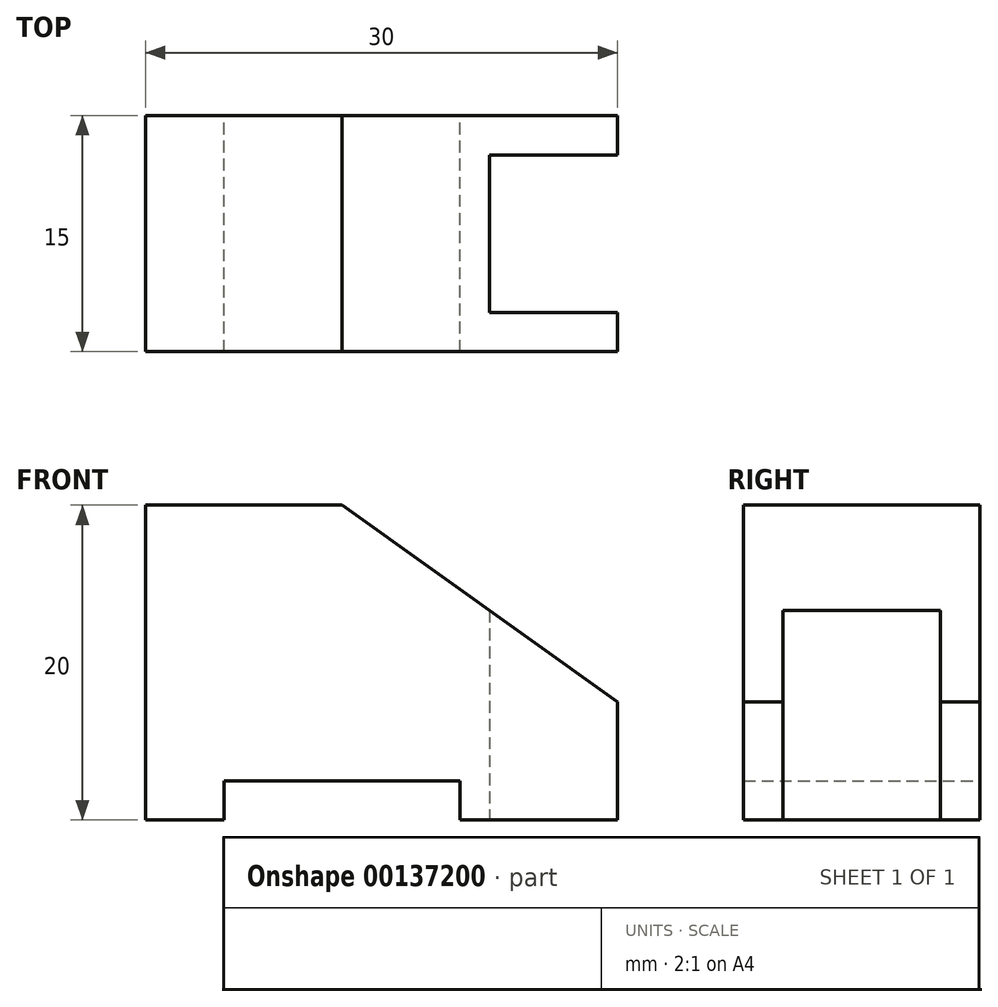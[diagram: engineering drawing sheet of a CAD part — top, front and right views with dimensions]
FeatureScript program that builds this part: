
annotation { "Feature Type Name" : "Feature", "Feature Type Description" : "" }
export const myFeature = defineFeature(function(context is Context, id is Id, definition is map)
    precondition{}
    {
        {
            var Q0;
            Q0=qCreatedBy(makeId("Front.planeOp"),FACE);
            var sketch = newSketch(context, id + "F0", { "sketchPlane" : qUnion([Q0])});
            skLineSegment(sketch, "E0", {"start": v(0, 0) * mm, "end": v(0, 20) * mm});
            skLineSegment(sketch, "E1", {"start": v(0, 20) * mm, "end": v(12.5, 20) * mm});
            skLineSegment(sketch, "E2", {"start": v(12.5, 20) * mm, "end": v(30, 7.5) * mm});
            skLineSegment(sketch, "E3", {"start": v(30, 7.5) * mm, "end": v(30, 0) * mm});
            skLineSegment(sketch, "E4", {"start": v(30, 0) * mm, "end": v(20, 0) * mm});
            skLineSegment(sketch, "E5", {"start": v(20, 0) * mm, "end": v(20, 2.5) * mm});
            skLineSegment(sketch, "E6", {"start": v(20, 2.5) * mm, "end": v(5, 2.5) * mm});
            skLineSegment(sketch, "E7", {"start": v(5, 2.5) * mm, "end": v(5, 0) * mm});
            skLineSegment(sketch, "E8", {"start": v(5, 0) * mm, "end": v(0, 0) * mm});
            skSolve(sketch);
        }
        {
            var Q0;
            Q0 = qSketchRegion(id + "F0", true);
            extrude(context, id + "F1", {"entities" : qUnion([Q0]), "depth" : 15 * mm});
        }
        {
            var Q0;
            Q0=qCreatedBy(makeId("Top.planeOp"),FACE);
            var sketch = newSketch(context, id + "F2", { "sketchPlane" : qUnion([Q0])});
            skLineSegment(sketch, "E9.0", {"start": v(21.86, -2.5) * mm, "end": v(21.86, -12.5) * mm});
            skLineSegment(sketch, "E10.0", {"start": v(30, -2.5) * mm, "end": v(21.86, -2.5) * mm});
            skLineSegment(sketch, "E11.0", {"start": v(30, -15) * mm, "end": v(30, 0) * mm});
            skLineSegment(sketch, "E12.0", {"start": v(21.86, -12.5) * mm, "end": v(30, -12.5) * mm});
            skSolve(sketch);
        }
        {
            var Q0;
            Q0 = qSketchRegion(id + "F2", true);
            extrude(context, id + "F3", {"entities" : qUnion([Q0]), "operationType" : NewBodyOperationType.REMOVE, "depth" : 25 * mm});
        }
    });
